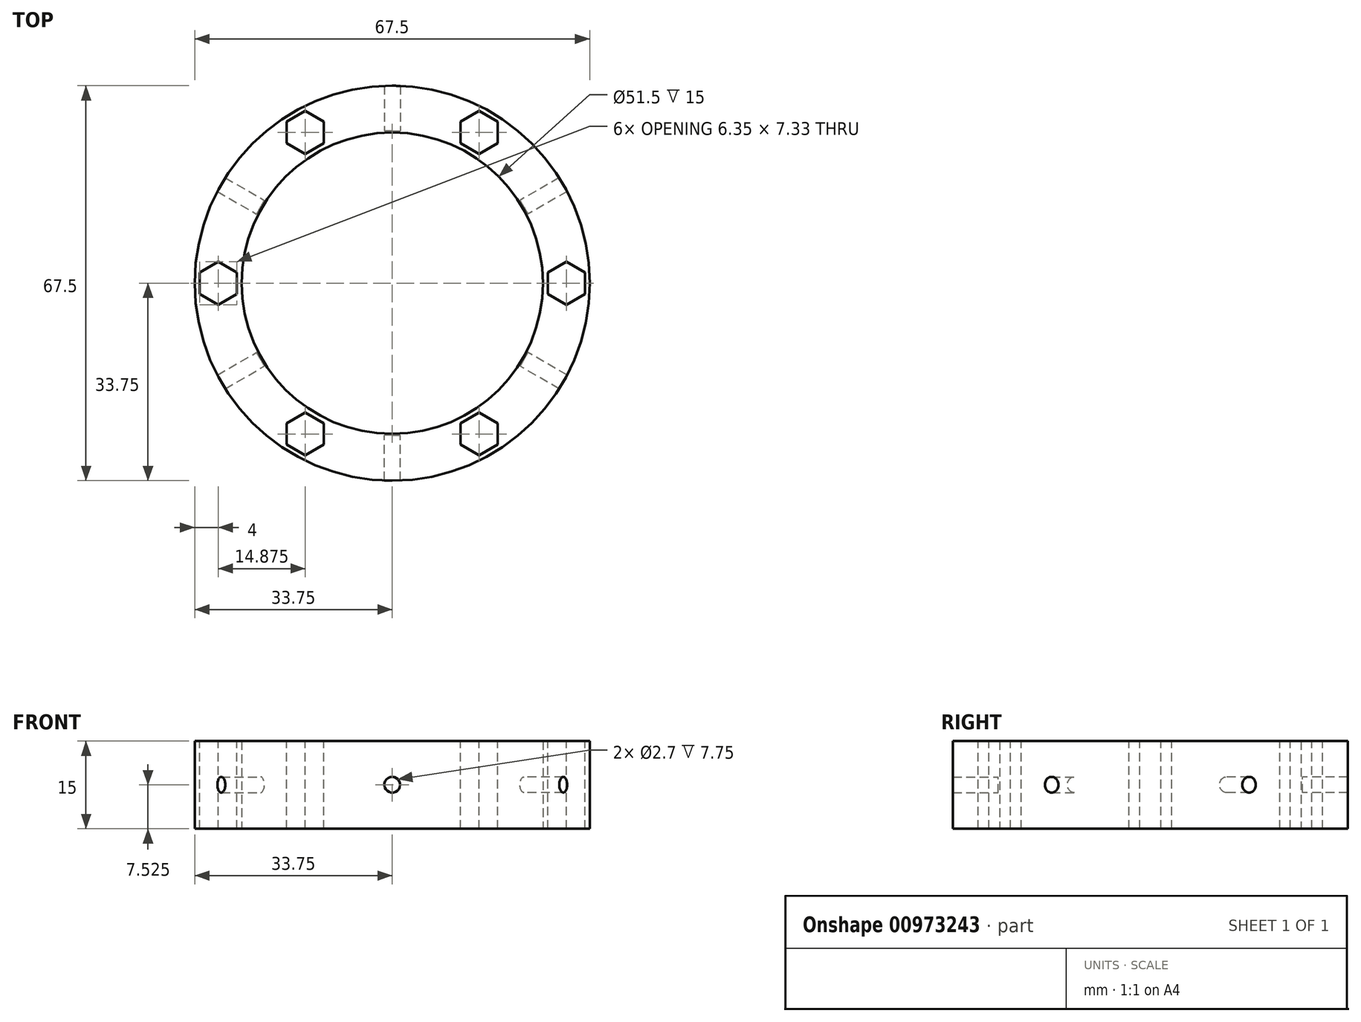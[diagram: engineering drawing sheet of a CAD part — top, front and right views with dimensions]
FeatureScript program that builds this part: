
annotation { "Feature Type Name" : "Feature", "Feature Type Description" : "" }
export const myFeature = defineFeature(function(context is Context, id is Id, definition is map)
    precondition{}
    {
        {
            var Q0;
            Q0=qCreatedBy(makeId("Top.planeOp"),FACE);
            var sketch = newSketch(context, id + "F0", { "sketchPlane" : qUnion([Q0])});
            skCircle(sketch, "E0", {"center": v(0, 0) * mm, "radius": 25.75 * mm});
            skCircle(sketch, "E1.0", {"center": v(0, 0) * mm, "radius": 33.75 * mm});
            skSolve(sketch);
        }
        {
            var Q0;
            Q0=makeQuery(id+"F0.imprint","IMPRINT",FACE,{"disambiguationData":[TD([[makeQuery(id+"F0.imprint","IMPRINT",EDGE,{"derivedFrom":sQuery(id+"F0.wireOp",EDGE,"E0")}),-1.0]])]});
            extrude(context, id + "F1", {"entities" : qUnion([Q0]), "depth" : 15 * mm, "offsetDistance" : 25 * mm});
        }
        {
            var Q0;
            Q0=makeQuery(id+"F1.opExtrude","CAP_FACE",FACE,{"disambiguationData":[OSD([sQuery(id+"F0.wireOp",EDGE,"E0"),sQuery(id+"F0.wireOp",EDGE,"E1.0")])],"isStart":false});
            var sketch = newSketch(context, id + "F2", { "sketchPlane" : qUnion([Q0])});
            skCircle(sketch, "E2.cCircle", {"center": v(-29.75, 0) * mm, "radius": 3.17 * mm, "construction": true});
            skLineSegment(sketch, "E2.0", {"start": v(-26.58, 1.83) * mm, "end": v(-26.58, -1.83) * mm});
            skLineSegment(sketch, "E2.1", {"start": v(-26.58, -1.83) * mm, "end": v(-29.75, -3.67) * mm});
            skLineSegment(sketch, "E2.2", {"start": v(-29.75, -3.67) * mm, "end": v(-32.92, -1.83) * mm});
            skLineSegment(sketch, "E2.3", {"start": v(-32.92, -1.83) * mm, "end": v(-32.92, 1.83) * mm});
            skLineSegment(sketch, "E2.4", {"start": v(-32.92, 1.83) * mm, "end": v(-29.75, 3.67) * mm});
            skLineSegment(sketch, "E2.5", {"start": v(-29.75, 3.67) * mm, "end": v(-26.58, 1.83) * mm});
            skPoint(sketch, "E2.0.midPoint", {"position": v(-26.58, 0) * mm});
            skLineSegment(sketch, "E3", {"start": v(-25.75, 0) * mm, "end": v(-26.58, 0) * mm, "construction": true});
            skLineSegment(sketch, "E4", {"start": v(-33.75, 0) * mm, "end": v(-32.92, 0) * mm, "construction": true});
            skSolve(sketch);
        }
        {
            var Q0;
            Q0=makeQuery(id+"F2.imprint","IMPRINT",FACE,{"disambiguationData":[TD([[makeQuery(id+"F2.imprint","IMPRINT",EDGE,{"derivedFrom":sQuery(id+"F2.wireOp",EDGE,"E2.0")}),-1.0]])]});
            extrude(context, id + "F3", {"entities" : qUnion([Q0]), "oppositeDirection" : true, "depth" : 20 * mm, "offsetDistance" : 25 * mm});
        }
        {
            var Q0;
            Q0=makeQuery(id+"F3.opExtrude","SWEPT_BODY",BODY,{"disambiguationData":[OSD([sQuery(id+"F2.wireOp",EDGE,"E2.0"),sQuery(id+"F2.wireOp",EDGE,"E2.1"),sQuery(id+"F2.wireOp",EDGE,"E2.2"),sQuery(id+"F2.wireOp",EDGE,"E2.3"),sQuery(id+"F2.wireOp",EDGE,"E2.4"),sQuery(id+"F2.wireOp",EDGE,"E2.5")])]});
            var Q1;
            Q1=makeQuery(id+"F1.opExtrude","CAP_EDGE",EDGE,{"disambiguationData":[OSD([sQuery(id+"F0.wireOp",EDGE,"E0")])],"isStart":false});
            circularPattern(context, id + "F4", {"entities" : qUnion([Q0]), "axis" : qUnion([Q1]), "angle" : 360 * degree, "instanceCount" : 6, "equalSpace" : true});
        }
        {
            var Q0;
            Q0=makeQuery(id+"F4.opPattern","COPY",BODY,{"derivedFrom":makeQuery(id+"F3.opExtrude","SWEPT_BODY",BODY,{"disambiguationData":[OSD([sQuery(id+"F2.wireOp",EDGE,"E2.0"),sQuery(id+"F2.wireOp",EDGE,"E2.1"),sQuery(id+"F2.wireOp",EDGE,"E2.2"),sQuery(id+"F2.wireOp",EDGE,"E2.3"),sQuery(id+"F2.wireOp",EDGE,"E2.4"),sQuery(id+"F2.wireOp",EDGE,"E2.5")])]}),"instanceName":"1"});
            var Q1;
            Q1=makeQuery(id+"F3.opExtrude","SWEPT_BODY",BODY,{"disambiguationData":[OSD([sQuery(id+"F2.wireOp",EDGE,"E2.0"),sQuery(id+"F2.wireOp",EDGE,"E2.1"),sQuery(id+"F2.wireOp",EDGE,"E2.2"),sQuery(id+"F2.wireOp",EDGE,"E2.3"),sQuery(id+"F2.wireOp",EDGE,"E2.4"),sQuery(id+"F2.wireOp",EDGE,"E2.5")])]});
            var Q2;
            Q2=makeQuery(id+"F4.opPattern","COPY",BODY,{"derivedFrom":makeQuery(id+"F3.opExtrude","SWEPT_BODY",BODY,{"disambiguationData":[OSD([sQuery(id+"F2.wireOp",EDGE,"E2.0"),sQuery(id+"F2.wireOp",EDGE,"E2.1"),sQuery(id+"F2.wireOp",EDGE,"E2.2"),sQuery(id+"F2.wireOp",EDGE,"E2.3"),sQuery(id+"F2.wireOp",EDGE,"E2.4"),sQuery(id+"F2.wireOp",EDGE,"E2.5")])]}),"instanceName":"2"});
            var Q3;
            Q3=makeQuery(id+"F4.opPattern","COPY",BODY,{"derivedFrom":makeQuery(id+"F3.opExtrude","SWEPT_BODY",BODY,{"disambiguationData":[OSD([sQuery(id+"F2.wireOp",EDGE,"E2.0"),sQuery(id+"F2.wireOp",EDGE,"E2.1"),sQuery(id+"F2.wireOp",EDGE,"E2.2"),sQuery(id+"F2.wireOp",EDGE,"E2.3"),sQuery(id+"F2.wireOp",EDGE,"E2.4"),sQuery(id+"F2.wireOp",EDGE,"E2.5")])]}),"instanceName":"3"});
            var Q4;
            Q4=makeQuery(id+"F4.opPattern","COPY",BODY,{"derivedFrom":makeQuery(id+"F3.opExtrude","SWEPT_BODY",BODY,{"disambiguationData":[OSD([sQuery(id+"F2.wireOp",EDGE,"E2.0"),sQuery(id+"F2.wireOp",EDGE,"E2.1"),sQuery(id+"F2.wireOp",EDGE,"E2.2"),sQuery(id+"F2.wireOp",EDGE,"E2.3"),sQuery(id+"F2.wireOp",EDGE,"E2.4"),sQuery(id+"F2.wireOp",EDGE,"E2.5")])]}),"instanceName":"4"});
            var Q5;
            Q5=makeQuery(id+"F4.opPattern","COPY",BODY,{"derivedFrom":makeQuery(id+"F3.opExtrude","SWEPT_BODY",BODY,{"disambiguationData":[OSD([sQuery(id+"F2.wireOp",EDGE,"E2.0"),sQuery(id+"F2.wireOp",EDGE,"E2.1"),sQuery(id+"F2.wireOp",EDGE,"E2.2"),sQuery(id+"F2.wireOp",EDGE,"E2.3"),sQuery(id+"F2.wireOp",EDGE,"E2.4"),sQuery(id+"F2.wireOp",EDGE,"E2.5")])]}),"instanceName":"5"});
            var Q6;
            Q6=makeQuery(id+"F1.opExtrude","SWEPT_BODY",BODY,{"disambiguationData":[OSD([sQuery(id+"F0.wireOp",EDGE,"E0"),sQuery(id+"F0.wireOp",EDGE,"E1.0")])]});
            booleanBodies(context, id + "F5", {"operationType" : BooleanOperationType.SUBTRACTION, "tools" : qUnion([Q0, Q1, Q2, Q3, Q4, Q5]), "targets" : qUnion([Q6])});
        }
        {
            var Q0;
            Q0=qCreatedBy(makeId("Front.planeOp"),FACE);
            var sketch = newSketch(context, id + "F6", { "sketchPlane" : qUnion([Q0])});
            skCircle(sketch, "E5", {"center": v(0, 7.52) * mm, "radius": 1.35 * mm});
            skLineSegment(sketch, "E6", {"start": v(0, 8.87) * mm, "end": v(0, 15.05) * mm, "construction": true});
            skLineSegment(sketch, "E7", {"start": v(0, 6.17) * mm, "end": v(0, 0) * mm, "construction": true});
            skSolve(sketch);
        }
        {
            var Q0;
            Q0=makeQuery(id+"F6.imprint","IMPRINT",FACE,{"disambiguationData":[TD([[makeQuery(id+"F6.imprint","IMPRINT",EDGE,{"derivedFrom":sQuery(id+"F6.wireOp",EDGE,"E5")}),1.0]])]});
            extrude(context, id + "F7", {"entities" : qUnion([Q0]), "depth" : 40 * mm, "offsetDistance" : 25 * mm});
        }
        {
            var Q0;
            Q0=makeQuery(id+"F7.opExtrude","SWEPT_BODY",BODY,{"disambiguationData":[OSD([sQuery(id+"F6.wireOp",EDGE,"E5")])]});
            transform(context, id + "F8", {"entities" : qUnion([Q0]), "transformType" : TransformType.TRANSLATION_3D, "dx" : 0 * mm, "dy" : -26 * mm, "dz" : 0 * mm, "makeCopy" : false});
        }
        {
            var Q0;
            Q0=makeQuery(id+"F7.opExtrude","SWEPT_BODY",BODY,{"disambiguationData":[OSD([sQuery(id+"F6.wireOp",EDGE,"E5")])]});
            var Q1;
            Q1=makeQuery(id+"F1.opExtrude","CAP_EDGE",EDGE,{"disambiguationData":[OSD([sQuery(id+"F0.wireOp",EDGE,"E0")])],"isStart":false});
            circularPattern(context, id + "F9", {"entities" : qUnion([Q0]), "axis" : qUnion([Q1]), "angle" : 360 * degree, "instanceCount" : 6, "equalSpace" : true});
        }
        {
            var Q0;
            Q0=makeQuery(id+"F7.opExtrude","SWEPT_BODY",BODY,{"disambiguationData":[OSD([sQuery(id+"F6.wireOp",EDGE,"E5")])]});
            var Q1;
            Q1=makeQuery(id+"F9.opPattern","COPY",BODY,{"derivedFrom":makeQuery(id+"F7.opExtrude","SWEPT_BODY",BODY,{"disambiguationData":[OSD([sQuery(id+"F6.wireOp",EDGE,"E5")])]}),"instanceName":"1"});
            var Q2;
            Q2=makeQuery(id+"F9.opPattern","COPY",BODY,{"derivedFrom":makeQuery(id+"F7.opExtrude","SWEPT_BODY",BODY,{"disambiguationData":[OSD([sQuery(id+"F6.wireOp",EDGE,"E5")])]}),"instanceName":"2"});
            var Q3;
            Q3=makeQuery(id+"F9.opPattern","COPY",BODY,{"derivedFrom":makeQuery(id+"F7.opExtrude","SWEPT_BODY",BODY,{"disambiguationData":[OSD([sQuery(id+"F6.wireOp",EDGE,"E5")])]}),"instanceName":"3"});
            var Q4;
            Q4=makeQuery(id+"F9.opPattern","COPY",BODY,{"derivedFrom":makeQuery(id+"F7.opExtrude","SWEPT_BODY",BODY,{"disambiguationData":[OSD([sQuery(id+"F6.wireOp",EDGE,"E5")])]}),"instanceName":"4"});
            var Q5;
            Q5=makeQuery(id+"F9.opPattern","COPY",BODY,{"derivedFrom":makeQuery(id+"F7.opExtrude","SWEPT_BODY",BODY,{"disambiguationData":[OSD([sQuery(id+"F6.wireOp",EDGE,"E5")])]}),"instanceName":"5"});
            var Q6;
            Q6=makeQuery(id+"F1.opExtrude","SWEPT_BODY",BODY,{"disambiguationData":[OSD([sQuery(id+"F0.wireOp",EDGE,"E0"),sQuery(id+"F0.wireOp",EDGE,"E1.0")])]});
            booleanBodies(context, id + "F10", {"operationType" : BooleanOperationType.SUBTRACTION, "tools" : qUnion([Q0, Q1, Q2, Q3, Q4, Q5]), "targets" : qUnion([Q6])});
        }
    });
